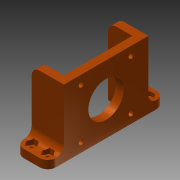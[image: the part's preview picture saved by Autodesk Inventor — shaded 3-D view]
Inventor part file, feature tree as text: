
AUTODESK INVENTOR PART (.ipt)
format: ipt  version: 2013 (Build 170138000, 138)  size: 225,280 bytes
history: native  units: mm
features: extrude x7, sketch x7, projected_geometry x2, fillet x1
ambient origin geometry x8: Origin, YZ Plane, XZ Plane, XY Plane, X Axis, Y Axis, Z Axis, Center Point
bodies: Solid1 (feature_tree)
feature tree (17):
  extrude  "Extrusion1"  Depth=5.0mm
  extrude  "Extrusion2"  Depth=20.0mm
  extrude  "Extrusion3"  Depth=22.1mm
  extrude  "Extrusion4"  Depth=31.0mm
  extrude  "Extrusion5"  Depth=42.0mm TaperAngle=0.0deg
  extrude  "Extrusion6"  Depth=10.0mm TaperAngle=0.0deg
  extrude  "Extrusion7"  Depth=10.0mm TaperAngle=0.0deg
  fillet  "Fillet1"  Radius=5.0mm
  sketch  "Sketch1"  dims[d0=42.5mm d2=5.0mm]
  sketch  "Sketch2"  dims[d3=5.0mm d4=20.0mm]
  sketch  "Sketch3"  dims[d5=42.0mm d6=0.0mm d7=22.1mm]
  sketch  "Sketch4"  dims[d9=42.0mm d10=0.0mm d11=31.0mm]
  sketch  "Sketch5"  dims[d12=3.1mm d13=42.0mm d14=0.0mm]
  sketch  "Sketch6"  dims[d15=5.0mm d17=10.0mm d18=0.0mm]
  projected_geometry  "Projected Loop1"
  sketch  "Sketch7"  dims[d19=5.0mm d21=10.0mm d22=0.0mm d26=5.0mm d27=3.1mm d28=10.0mm d29=0.0mm d31=5.6mm d32=2.5mm d33=0.0mm d34=5.0mm]
  projected_geometry  "Projected Loop2"
